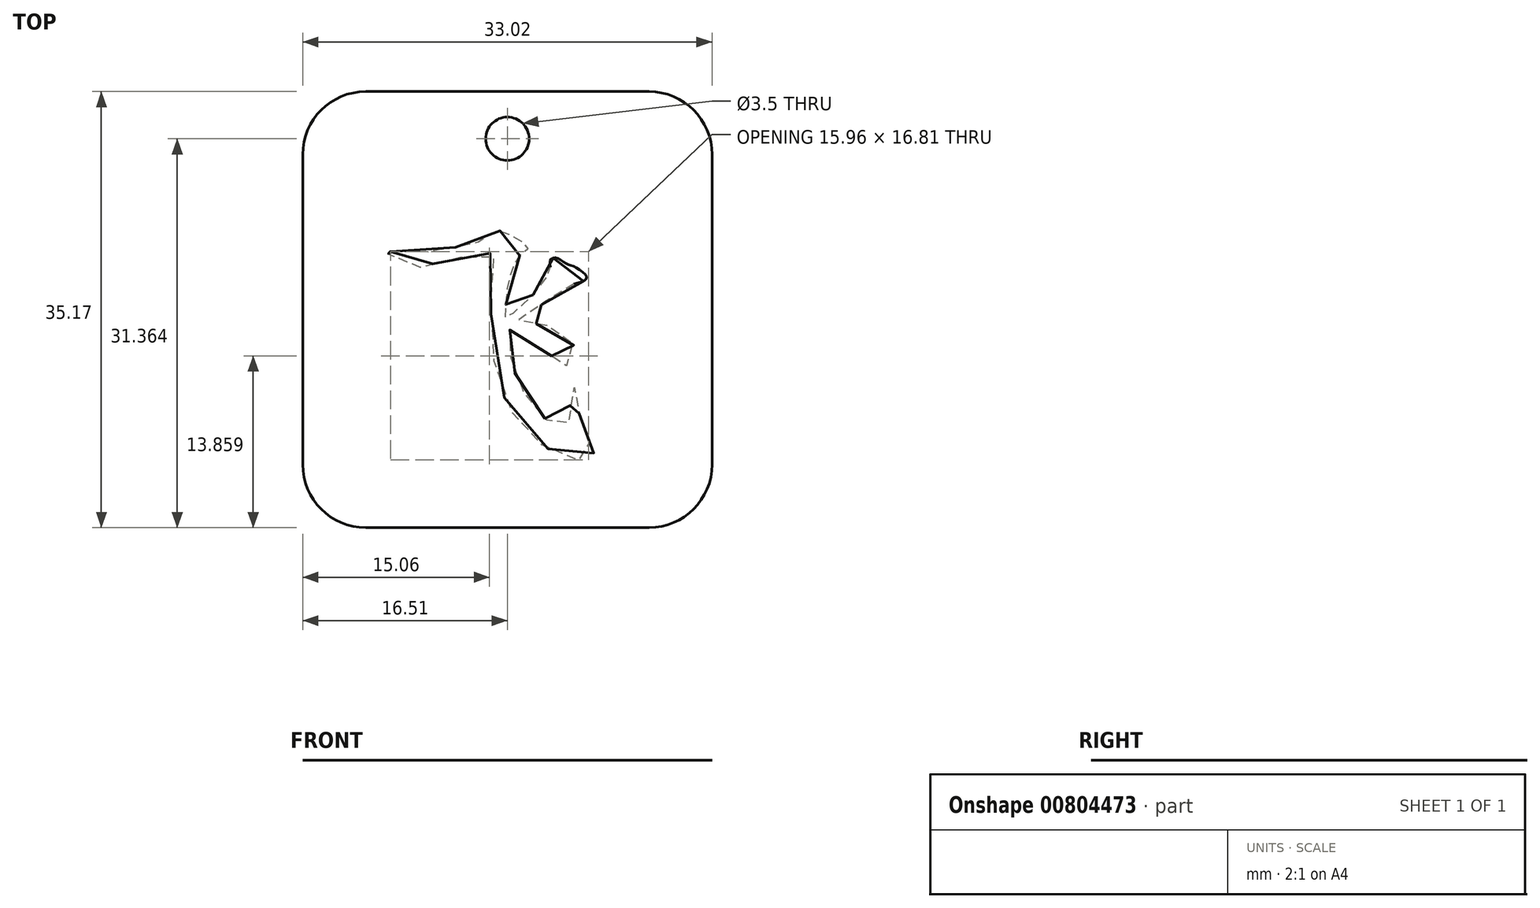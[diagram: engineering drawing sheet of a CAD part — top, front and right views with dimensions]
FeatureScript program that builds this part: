
annotation { "Feature Type Name" : "Feature", "Feature Type Description" : "" }
export const myFeature = defineFeature(function(context is Context, id is Id, definition is map)
    precondition{}
    {
        {
            var Q0;
            Q0=qCreatedBy(makeId("Top.planeOp"),FACE);
            var sketch = newSketch(context, id + "F0", { "sketchPlane" : qUnion([Q0])});
            skLineSegment(sketch, "E0.bottom", {"start": v(16.5, -19.79) * mm, "end": v(-16.5, -19.79) * mm});
            skLineSegment(sketch, "E0.top", {"start": v(16.51, 15.38) * mm, "end": v(-16.51, 15.38) * mm});
            skLineSegment(sketch, "E0.left", {"start": v(16.51, -19.79) * mm, "end": v(16.51, 15.38) * mm});
            skLineSegment(sketch, "E0.right", {"start": v(-16.51, -19.79) * mm, "end": v(-16.5, 15.38) * mm});
            skPoint(sketch, "E0.middle", {"position": v(-1.52, -5.38) * mm});
            skCircle(sketch, "E1", {"center": v(0, 11.57) * mm, "radius": 1.75 * mm});
            skFitSpline(sketch, "E2", {"points": [v(-9.43, 2.47) * mm, v(-6.7, 2.46) * mm, v(-5.32, 2.7) * mm, v(-3.97, 2.87) * mm, v(-3.18, 3.08) * mm, v(-1.94, 3.46) * mm, v(-1.04, 4.16) * mm, v(-0.1, 3.98) * mm, v(0.82, 3.5) * mm, v(1.7, 2.8) * mm, v(1.32, 2.42) * mm, v(0.71, 1.85) * mm, v(0.3, 0.7) * mm, v(0.03, -0.25) * mm, v(-0.13, -1.79) * mm, v(-0.14, -2.87) * mm, v(0.72, -2.25) * mm, v(1.6, -1.47) * mm, v(2.32, -0.73) * mm, v(2.88, 0.11) * mm, v(3.45, 0.82) * mm, v(3.45, 1.74) * mm, v(3.84, 1.98) * mm, v(4.76, 1.51) * mm, v(5.47, 1.22) * mm, v(6.38, 0.43) * mm, v(6.09, 0.06) * mm, v(5.22, -0.19) * mm, v(4.21, -0.87) * mm, v(3.18, -1.47) * mm, v(2.34, -2.13) * mm, v(1.2, -2.77) * mm, v(0.91, -3.02) * mm, v(1.58, -3.16) * mm, v(2.61, -3.39) * mm, v(3.4, -3.53) * mm, v(4.12, -3.95) * mm, v(4.93, -4.5) * mm, v(5.47, -5.38) * mm, v(5.5, -6.17) * mm, v(5.08, -6.66) * mm, v(4.34, -6.66) * mm, v(3.33, -5.73) * mm, v(2.32, -5.11) * mm, v(1.28, -4.42) * mm, v(0.52, -4.02) * mm, v(-0.04, -3.8) * mm, v(0, -4.8) * mm, v(0.22, -5.9) * mm, v(0.5, -7) * mm, v(1.06, -8.43) * mm, v(1.85, -9.7) * mm, v(2.61, -10.53) * mm, v(3.45, -11.32) * mm, v(4.31, -11.64) * mm, v(4.8, -11.73) * mm, v(5, -10.6) * mm, v(5.17, -9.2) * mm, v(5.4, -8.48) * mm, v(5.59, -8.79) * mm, v(5.72, -10.1) * mm, v(5.86, -10.84) * mm, v(5.96, -11.47) * mm, v(6.17, -12.03) * mm, v(6.66, -12.9) * mm, v(6.97, -13.89) * mm, v(6.57, -14.33) * mm, v(5.25, -14.28) * mm, v(3.86, -13.8) * mm, v(2.5, -12.88) * mm, v(1.39, -11.9) * mm, v(-0.15, -9.52) * mm, v(-0.99, -6.84) * mm, v(-1.32, -3.24) * mm, v(-1.25, 0.27) * mm, v(-1.15, 1.53) * mm, v(-1.18, 2.25) * mm, v(-2.48, 2.26) * mm, v(-3.85, 1.97) * mm, v(-5.32, 1.65) * mm, v(-7.12, 1.18) * mm, v(-8.4, 1.15) * mm, v(-9.54, 2.15) * mm, v(-9.43, 2.47) * mm]});
            skLineSegment(sketch, "E3", {"start": v(0, 11.57) * mm, "end": v(0, 15.38) * mm, "construction": true});
            skLineSegment(sketch, "E4", {"start": v(0, 0) * mm, "end": v(0, 11.57) * mm, "construction": true});
            skSolve(sketch);
        }
        {
            var Q0;
            Q0 = qSketchRegion(id + "F0", true);
            extrude(context, id + "F1", {"entities" : qUnion([Q0]), "depth" : 1 / 203.2 * mm, "offsetDistance" : 25.4 * mm});
        }
        {
            var Q0;
            Q0=makeQuery(id+"F1.opExtrude","SWEPT_EDGE",EDGE,{"disambiguationData":[OSD([sQuery(id+"F0.wireOp",EDGE,"E0.top"),sQuery(id+"F0.wireOp",EDGE,"E0.right")])]});
            var Q1;
            Q1=makeQuery(id+"F1.opExtrude","SWEPT_EDGE",EDGE,{"disambiguationData":[OSD([sQuery(id+"F0.wireOp",EDGE,"E0.top"),sQuery(id+"F0.wireOp",EDGE,"E0.left")])]});
            var Q2;
            Q2=makeQuery(id+"F1.opExtrude","SWEPT_EDGE",EDGE,{"disambiguationData":[OSD([sQuery(id+"F0.wireOp",EDGE,"E0.bottom"),sQuery(id+"F0.wireOp",EDGE,"E0.left")])]});
            var Q3;
            Q3=makeQuery(id+"F1.opExtrude","SWEPT_EDGE",EDGE,{"disambiguationData":[OSD([sQuery(id+"F0.wireOp",EDGE,"E0.bottom"),sQuery(id+"F0.wireOp",EDGE,"E0.right")])]});
            fillet(context, id + "F2", {"entities" : qUnion([Q0, Q1, Q2, Q3]), "radius" : 5.08 * mm, "tangentPropagation" : true, "allowEdgeOverflow" : false});
        }
    });
